# Revit family: Sanitary_Showers_hansgrohe_26900SGP-Vernis-Shape-Showerpipe-240-1je_NEW
name_source: partatom
category: Plumbing Fixtures
revit_build: Autodesk Revit 2018 (Build: 20170223_1515(x64)
units: mm (PartAtom-declared; Revit-internal decimal feet)

## family parameters
Cut with Voids When Loaded = Yes
Host = Face
OmniClass Number = 23.31.17.00
OmniClass Title = Showers
Part Type = Normal
Room Calculation Point = No
Round Connector Dimension = Use Diameter
Shared = No

## types (1)
- 679 Matte Black
    Always visible = Yes
    BIMobject category = Showers
    Connector Description = Water Inlet 12.7 mm
    Default Elevation = 1219 mm
    Description = Vernis Shape Showerpipe 240 1jet 2 ticks with bath thermostat
    Design country = Germany
    Diameter = 13 mm
    EAN code = 4059625425299
    Edition number = 1
    IFC Classification = Sanitary Terminal
    Manufacturer = Hansgrohe
    Manufacturer country = Germany
    Manufacturer name = hansgrohe
    Masterformat 2014 Code = 22 41 23
    Masterformat 2014 Description = Residential Showers
    Material = Hansgrohe - Metal - 679 Matte Black
    Model = 26900SGP
    OmniClass Code = 23-31 17 00
    OmniClass Description = Showers
    Product Guid = d47f2e0a-e971-4aa9-96cb-fa93291d6aac
    Product SKU = 26900SGP
    Product data url = https://bimobject.com
    Product family = Showerpipes with thermostat
    Product group = Vernis Shape
    Product name = 26900SGP Vernis Shape Showerpipe 240 1jet 2 ticks with bath thermostat
    Product url = https://pro.hansgrohe.com
    QR code = https://bimobject.com
    UNSPSC Code = 30181503
    URL = https://www.hansgrohe.com
    Uniclass 2015 Code = Pr_40_20_87_76
    Uniclass 2015 Name = Shower heads
    Uniformat II Code = D2010
    Uniformat II Description = Plumbing Fixtures
    Version = 1
    Weight Net (Kg) = 4.2

## geometry (parser evidence)
native form markers: Sweep x2
no freeform markers — native parametric forms only
